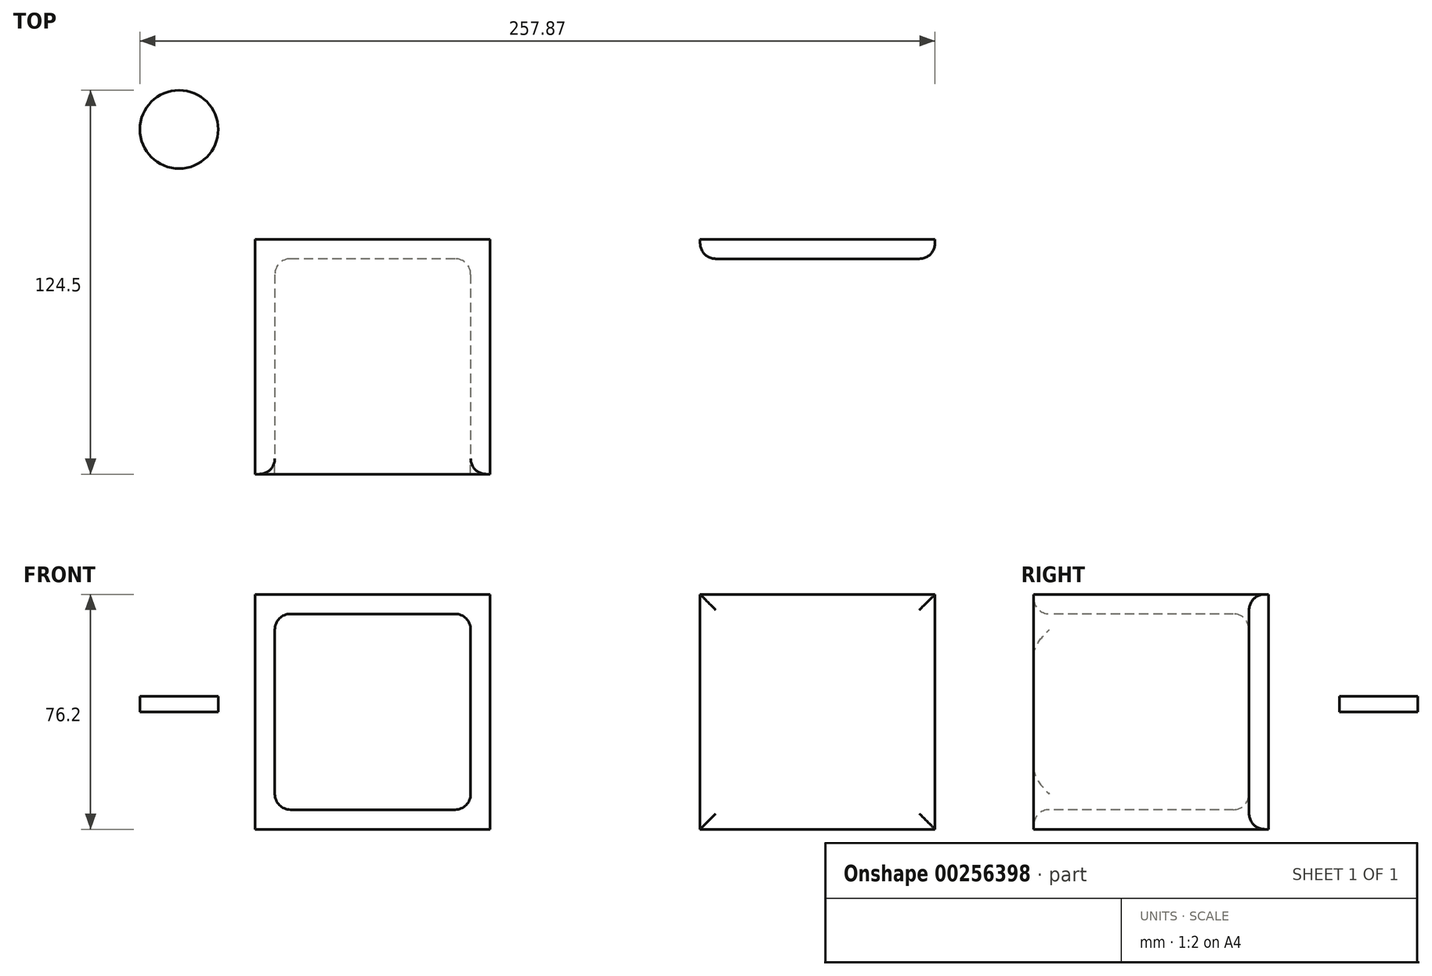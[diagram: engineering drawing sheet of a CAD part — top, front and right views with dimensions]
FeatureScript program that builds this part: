
annotation { "Feature Type Name" : "Feature", "Feature Type Description" : "" }
export const myFeature = defineFeature(function(context is Context, id is Id, definition is map)
    precondition{}
    {
        {
            var Q0;
            Q0=qCreatedBy(makeId("Front.planeOp"),FACE);
            var sketch = newSketch(context, id + "F0", { "sketchPlane" : qUnion([Q0])});
            skLineSegment(sketch, "E0.bottom", {"start": v(38.1, -38.1) * mm, "end": v(-38.1, -38.1) * mm});
            skLineSegment(sketch, "E0.top", {"start": v(38.1, 38.1) * mm, "end": v(-38.1, 38.1) * mm});
            skLineSegment(sketch, "E0.left", {"start": v(38.1, -38.1) * mm, "end": v(38.1, 38.1) * mm});
            skLineSegment(sketch, "E0.right", {"start": v(-38.1, -38.1) * mm, "end": v(-38.1, 38.1) * mm});
            skPoint(sketch, "E0.middle", {"position": v(0, 0) * mm});
            skLineSegment(sketch, "E1.bottom", {"start": v(182.35, 38.1) * mm, "end": v(106.15, 38.1) * mm});
            skLineSegment(sketch, "E1.top", {"start": v(182.35, -38.1) * mm, "end": v(106.15, -38.1) * mm});
            skLineSegment(sketch, "E1.left", {"start": v(182.35, 38.1) * mm, "end": v(182.35, -38.1) * mm});
            skLineSegment(sketch, "E1.right", {"start": v(106.15, 38.1) * mm, "end": v(106.15, -38.1) * mm});
            skPoint(sketch, "E1.middle", {"position": v(144.25, 0) * mm});
            skSolve(sketch);
        }
        {
            var Q0;
            Q0=makeQuery(id+"F0.imprint","IMPRINT",FACE,{"disambiguationData":[TD([[makeQuery(id+"F0.imprint","IMPRINT",EDGE,{"derivedFrom":sQuery(id+"F0.wireOp",EDGE,"E0.bottom")}),-1.0]])]});
            extrude(context, id + "F1", {"entities" : qUnion([Q0]), "depth" : 76.2 * mm});
        }
        {
            var Q0;
            Q0=makeQuery(id+"F1.opExtrude","CAP_FACE",FACE,{"disambiguationData":[OSD([sQuery(id+"F0.wireOp",EDGE,"E0.bottom"),sQuery(id+"F0.wireOp",EDGE,"E0.top"),sQuery(id+"F0.wireOp",EDGE,"E0.left"),sQuery(id+"F0.wireOp",EDGE,"E0.right")])],"isStart":false});
            var sketch = newSketch(context, id + "F2", { "sketchPlane" : qUnion([Q0])});
            skLineSegment(sketch, "E2.bottom", {"start": v(31.75, 31.75) * mm, "end": v(-31.75, 31.75) * mm});
            skLineSegment(sketch, "E2.top", {"start": v(31.75, -31.75) * mm, "end": v(-31.75, -31.75) * mm});
            skLineSegment(sketch, "E2.left", {"start": v(31.75, 31.75) * mm, "end": v(31.75, -31.75) * mm});
            skLineSegment(sketch, "E2.right", {"start": v(-31.75, 31.75) * mm, "end": v(-31.75, -31.75) * mm});
            skPoint(sketch, "E2.middle", {"position": v(0, 0) * mm});
            skSolve(sketch);
        }
        {
            var Q0;
            Q0=makeQuery(id+"F2.imprint","IMPRINT",FACE,{"disambiguationData":[TD([[makeQuery(id+"F2.imprint","IMPRINT",EDGE,{"derivedFrom":sQuery(id+"F2.wireOp",EDGE,"E2.bottom")}),1.0]])]});
            extrude(context, id + "F3", {"entities" : qUnion([Q0]), "operationType" : NewBodyOperationType.REMOVE, "oppositeDirection" : true, "depth" : 69.85 * mm});
        }
        {
            var Q0;
            Q0=makeQuery(id+"F0.imprint","IMPRINT",FACE,{"disambiguationData":[TD([[makeQuery(id+"F0.imprint","IMPRINT",EDGE,{"derivedFrom":sQuery(id+"F0.wireOp",EDGE,"E1.bottom")}),1.0]])]});
            extrude(context, id + "F4", {"entities" : qUnion([Q0]), "depth" : 6.35 * mm});
        }
        {
            var Q0;
            Q0=makeQuery(id+"F4.opExtrude","CAP_FACE",FACE,{"disambiguationData":[OSD([sQuery(id+"F0.wireOp",EDGE,"E1.bottom"),sQuery(id+"F0.wireOp",EDGE,"E1.top"),sQuery(id+"F0.wireOp",EDGE,"E1.left"),sQuery(id+"F0.wireOp",EDGE,"E1.right")])],"isStart":false});
            fillet(context, id + "F5", {"entities" : qUnion([Q0]), "radius" : 5.08 * mm, "tangentPropagation" : true, "allowEdgeOverflow" : false});
        }
        {
            var Q0;
            Q0=makeQuery(id+"F3.boolean.opBoolean","COPY",FACE,{"derivedFrom":makeQuery(id+"F3.opExtrude","SWEPT_FACE",FACE,{"disambiguationData":[OSD([sQuery(id+"F2.wireOp",EDGE,"E2.bottom")])]})});
            var Q1;
            Q1=makeQuery(id+"F3.boolean.opBoolean","COPY",FACE,{"derivedFrom":makeQuery(id+"F3.opExtrude","SWEPT_FACE",FACE,{"disambiguationData":[OSD([sQuery(id+"F2.wireOp",EDGE,"E2.top")])]})});
            fillet(context, id + "F6", {"entities" : qUnion([Q0, Q1]), "radius" : 5.08 * mm, "tangentPropagation" : true, "allowEdgeOverflow" : false});
        }
        {
            var Q0;
            Q0=qCreatedBy(makeId("Top.planeOp"),FACE);
            var sketch = newSketch(context, id + "F7", { "sketchPlane" : qUnion([Q0])});
            skCircle(sketch, "E3", {"center": v(-62.82, 35.6) * mm, "radius": 12.7 * mm});
            skSolve(sketch);
        }
        {
            var Q0;
            Q0=makeQuery(id+"F7.imprint","IMPRINT",FACE,{"disambiguationData":[TD([[makeQuery(id+"F7.imprint","IMPRINT",EDGE,{"derivedFrom":sQuery(id+"F7.wireOp",EDGE,"E3")}),1.0]])]});
            extrude(context, id + "F8", {"entities" : qUnion([Q0]), "depth" : 5.08 * mm});
        }
        {
            var Q0;
            Q0=makeQuery(id+"F3.boolean.opBoolean","COPY",EDGE,{"derivedFrom":makeQuery(id+"F3.opExtrude","CAP_EDGE",EDGE,{"disambiguationData":[OSD([sQuery(id+"F2.wireOp",EDGE,"E2.right")])],"isStart":false})});
            var Q1;
            Q1=makeQuery(id+"F3.boolean.opBoolean","COPY",EDGE,{"derivedFrom":makeQuery(id+"F3.opExtrude","CAP_EDGE",EDGE,{"disambiguationData":[OSD([sQuery(id+"F2.wireOp",EDGE,"E2.left")])],"isStart":false})});
            fillet(context, id + "F9", {"entities" : qUnion([Q0, Q1]), "radius" : 5.08 * mm, "tangentPropagation" : true, "allowEdgeOverflow" : false});
        }
    });
